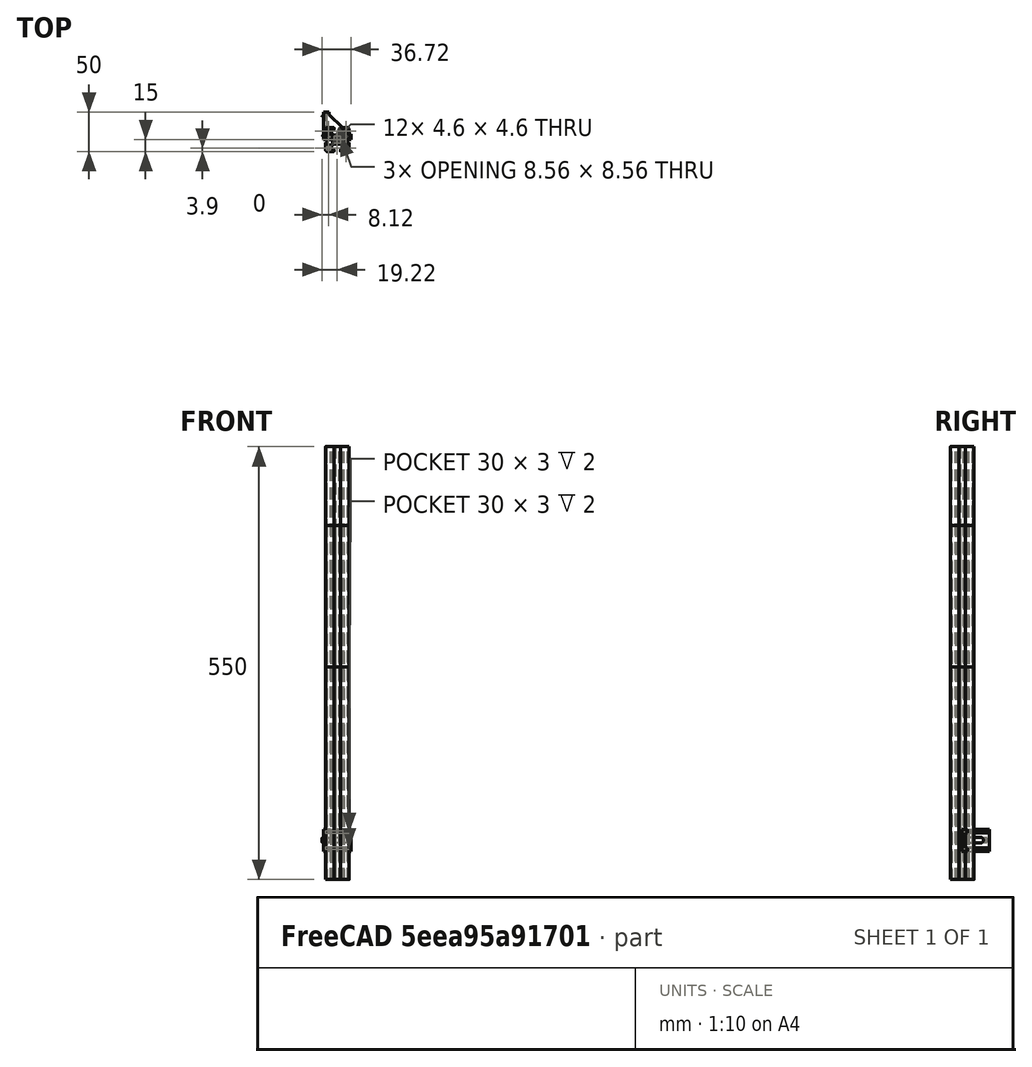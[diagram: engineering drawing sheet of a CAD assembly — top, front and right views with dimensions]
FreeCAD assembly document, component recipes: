
FREECAD ASSEMBLY — COMPONENT RECIPES ("frame")

This assembly document has 67 components, labeled P0..P66 below (a component is one placed body or linked part). 0 of them carry a construction recipe — the FreeCAD feature program that regenerates the part from scratch, quoted from this document or its linked companion documents; the rest are supplied as boundary geometry only. No exploded tour is included for this assembly.
COMPONENT P0 — geometry summary ("30-30 ANGLE BRACKET 002"; no construction recipe available for this part):
  bounding box: 36.7 x 36.7 x 28.0 mm
  tessellated surface: 876 triangles
  volume: 10483 mm^3 (28% of its bounding box)
  symmetry: mirror-symmetric across its y mid-plane
COMPONENT P1 — geometry summary ("30-30 ANGLE BRACKET 003"; no construction recipe available for this part):
  bounding box: 36.7 x 36.7 x 28.0 mm
  tessellated surface: 876 triangles
  volume: 10483 mm^3 (28% of its bounding box)
  symmetry: mirror-symmetric across its y mid-plane
COMPONENT P2 — geometry summary ("30-30 ANGLE BRACKET 004"; no construction recipe available for this part):
  bounding box: 36.7 x 36.7 x 28.0 mm
  tessellated surface: 876 triangles
  volume: 10483 mm^3 (28% of its bounding box)
  symmetry: mirror-symmetric across its y mid-plane
COMPONENT P3 — geometry summary ("30-30 ANGLE BRACKET 005"; no construction recipe available for this part):
  bounding box: 36.7 x 36.7 x 28.0 mm
  tessellated surface: 876 triangles
  volume: 10483 mm^3 (28% of its bounding box)
  symmetry: mirror-symmetric across its y mid-plane
COMPONENT P4 — geometry summary ("30-30 ANGLE BRACKET 006"; no construction recipe available for this part):
  bounding box: 36.7 x 36.7 x 28.0 mm
  tessellated surface: 876 triangles
  volume: 10483 mm^3 (28% of its bounding box)
  symmetry: mirror-symmetric across its y mid-plane
COMPONENT P5 — geometry summary ("30-30 ANGLE BRACKET 007"; no construction recipe available for this part):
  bounding box: 36.7 x 36.7 x 28.0 mm
  tessellated surface: 876 triangles
  volume: 10483 mm^3 (28% of its bounding box)
  symmetry: mirror-symmetric across its y mid-plane
COMPONENT P6 — geometry summary ("30-30 ANGLE BRACKET 008"; no construction recipe available for this part):
  bounding box: 36.7 x 36.7 x 28.0 mm
  tessellated surface: 876 triangles
  volume: 10483 mm^3 (28% of its bounding box)
  symmetry: mirror-symmetric across its y mid-plane
COMPONENT P7 — geometry summary ("30-30 ANGLE BRACKET 009"; no construction recipe available for this part):
  bounding box: 36.7 x 36.7 x 28.0 mm
  tessellated surface: 876 triangles
  volume: 10483 mm^3 (28% of its bounding box)
  symmetry: mirror-symmetric across its y mid-plane
COMPONENT P8 — geometry summary ("30-30 ANGLE BRACKET 010"; no construction recipe available for this part):
  bounding box: 36.7 x 36.7 x 28.0 mm
  tessellated surface: 876 triangles
  volume: 10483 mm^3 (28% of its bounding box)
  symmetry: mirror-symmetric across its y mid-plane
COMPONENT P9 — geometry summary ("30-30 ANGLE BRACKET 011"; no construction recipe available for this part):
  bounding box: 36.7 x 36.7 x 28.0 mm
  tessellated surface: 876 triangles
  volume: 10483 mm^3 (28% of its bounding box)
  symmetry: mirror-symmetric across its y mid-plane
COMPONENT P10 — geometry summary ("30-30 ANGLE BRACKET 012"; no construction recipe available for this part):
  bounding box: 36.7 x 36.7 x 28.0 mm
  tessellated surface: 876 triangles
  volume: 10483 mm^3 (28% of its bounding box)
  symmetry: mirror-symmetric across its y mid-plane
COMPONENT P11 — geometry summary ("30-30 ANGLE BRACKET 013"; no construction recipe available for this part):
  bounding box: 36.7 x 36.7 x 28.0 mm
  tessellated surface: 876 triangles
  volume: 10483 mm^3 (28% of its bounding box)
  symmetry: mirror-symmetric across its y mid-plane
COMPONENT P12 — geometry summary ("30-30 ANGLE BRACKET 014"; no construction recipe available for this part):
  bounding box: 36.7 x 36.7 x 28.0 mm
  tessellated surface: 876 triangles
  volume: 10483 mm^3 (28% of its bounding box)
  symmetry: mirror-symmetric across its y mid-plane
COMPONENT P13 — geometry summary ("30-30 ANGLE BRACKET 015"; no construction recipe available for this part):
  bounding box: 36.7 x 36.7 x 28.0 mm
  tessellated surface: 876 triangles
  volume: 10483 mm^3 (28% of its bounding box)
  symmetry: mirror-symmetric across its y mid-plane
COMPONENT P14 — geometry summary ("30-30 ANGLE BRACKET 016"; no construction recipe available for this part):
  bounding box: 36.7 x 36.7 x 28.0 mm
  tessellated surface: 876 triangles
  volume: 10483 mm^3 (28% of its bounding box)
  symmetry: mirror-symmetric across its y mid-plane
COMPONENT P15 — geometry summary ("30-30 ANGLE BRACKET 017"; no construction recipe available for this part):
  bounding box: 36.7 x 36.7 x 28.0 mm
  tessellated surface: 876 triangles
  volume: 10483 mm^3 (28% of its bounding box)
  symmetry: mirror-symmetric across its y mid-plane
COMPONENT P16 — geometry summary ("30-30 ANGLE BRACKET 018"; no construction recipe available for this part):
  bounding box: 36.7 x 36.7 x 28.0 mm
  tessellated surface: 876 triangles
  volume: 10483 mm^3 (28% of its bounding box)
  symmetry: mirror-symmetric across its y mid-plane
COMPONENT P17 — geometry summary ("30-30 ANGLE BRACKET 019"; no construction recipe available for this part):
  bounding box: 36.7 x 36.7 x 28.0 mm
  tessellated surface: 876 triangles
  volume: 10483 mm^3 (28% of its bounding box)
  symmetry: mirror-symmetric across its y mid-plane
COMPONENT P18 — geometry summary ("30-30 ANGLE BRACKET 020"; no construction recipe available for this part):
  bounding box: 36.7 x 36.7 x 28.0 mm
  tessellated surface: 876 triangles
  volume: 10483 mm^3 (28% of its bounding box)
  symmetry: mirror-symmetric across its y mid-plane
COMPONENT P19 — geometry summary ("30-30 ANGLE BRACKET 021"; no construction recipe available for this part):
  bounding box: 36.7 x 36.7 x 28.0 mm
  tessellated surface: 876 triangles
  volume: 10483 mm^3 (28% of its bounding box)
  symmetry: mirror-symmetric across its y mid-plane
COMPONENT P20 — geometry summary ("30-30 ANGLE BRACKET 022"; no construction recipe available for this part):
  bounding box: 36.7 x 36.7 x 28.0 mm
  tessellated surface: 876 triangles
  volume: 10483 mm^3 (28% of its bounding box)
  symmetry: mirror-symmetric across its y mid-plane
COMPONENT P21 — geometry summary ("30-30 ANGLE BRACKET 023"; no construction recipe available for this part):
  bounding box: 36.7 x 36.7 x 28.0 mm
  tessellated surface: 876 triangles
  volume: 10483 mm^3 (28% of its bounding box)
  symmetry: mirror-symmetric across its y mid-plane
COMPONENT P22 — geometry summary ("30-30 ANGLE BRACKET 024"; no construction recipe available for this part):
  bounding box: 36.7 x 36.7 x 28.0 mm
  tessellated surface: 876 triangles
  volume: 10483 mm^3 (28% of its bounding box)
  symmetry: mirror-symmetric across its y mid-plane
COMPONENT P23 — geometry summary ("30-30 ANGLE BRACKET 025"; no construction recipe available for this part):
  bounding box: 36.7 x 36.7 x 28.0 mm
  tessellated surface: 876 triangles
  volume: 10483 mm^3 (28% of its bounding box)
  symmetry: mirror-symmetric across its y mid-plane
COMPONENT P24 — geometry summary ("30-30 ANGLE BRACKET 026"; no construction recipe available for this part):
  bounding box: 36.7 x 36.7 x 28.0 mm
  tessellated surface: 876 triangles
  volume: 10483 mm^3 (28% of its bounding box)
  symmetry: mirror-symmetric across its y mid-plane
COMPONENT P25 — geometry summary ("30-30 ANGLE BRACKET 027"; no construction recipe available for this part):
  bounding box: 36.7 x 36.7 x 28.0 mm
  tessellated surface: 876 triangles
  volume: 10483 mm^3 (28% of its bounding box)
  symmetry: mirror-symmetric across its y mid-plane
COMPONENT P26 — geometry summary ("30-30 ANGLE BRACKET 028"; no construction recipe available for this part):
  bounding box: 36.7 x 36.7 x 28.0 mm
  tessellated surface: 876 triangles
  volume: 10483 mm^3 (28% of its bounding box)
  symmetry: mirror-symmetric across its y mid-plane
COMPONENT P27 — geometry summary ("30-30 ANGLE BRACKET 029"; no construction recipe available for this part):
  bounding box: 36.7 x 36.7 x 28.0 mm
  tessellated surface: 876 triangles
  volume: 10483 mm^3 (28% of its bounding box)
  symmetry: mirror-symmetric across its y mid-plane
COMPONENT P28 — geometry summary ("30-30 ANGLE BRACKET 030"; no construction recipe available for this part):
  bounding box: 36.7 x 36.7 x 28.0 mm
  tessellated surface: 876 triangles
  volume: 10483 mm^3 (28% of its bounding box)
  symmetry: mirror-symmetric across its y mid-plane
COMPONENT P29 — geometry summary ("30-30 ANGLE BRACKET 031"; no construction recipe available for this part):
  bounding box: 36.7 x 36.7 x 28.0 mm
  tessellated surface: 876 triangles
  volume: 10483 mm^3 (28% of its bounding box)
  symmetry: mirror-symmetric across its y mid-plane
COMPONENT P30 — geometry summary ("30-30 ANGLE BRACKET 032"; no construction recipe available for this part):
  bounding box: 36.7 x 36.7 x 28.0 mm
  tessellated surface: 876 triangles
  volume: 10483 mm^3 (28% of its bounding box)
  symmetry: mirror-symmetric across its y mid-plane
COMPONENT P31 — geometry summary ("30-30 ANGLE BRACKET 033"; no construction recipe available for this part):
  bounding box: 36.7 x 36.7 x 28.0 mm
  tessellated surface: 876 triangles
  volume: 10483 mm^3 (28% of its bounding box)
  symmetry: mirror-symmetric across its y mid-plane
COMPONENT P32 — geometry summary ("30-30 ANGLE BRACKET 034"; no construction recipe available for this part):
  bounding box: 36.7 x 36.7 x 28.0 mm
  tessellated surface: 876 triangles
  volume: 10483 mm^3 (28% of its bounding box)
  symmetry: mirror-symmetric across its y mid-plane
COMPONENT P33 — geometry summary ("30-30 ANGLE BRACKET 035"; no construction recipe available for this part):
  bounding box: 36.7 x 36.7 x 28.0 mm
  tessellated surface: 876 triangles
  volume: 10483 mm^3 (28% of its bounding box)
  symmetry: mirror-symmetric across its y mid-plane
COMPONENT P34 — geometry summary ("30-30 ANGLE BRACKET 036"; no construction recipe available for this part):
  bounding box: 36.7 x 36.7 x 28.0 mm
  tessellated surface: 876 triangles
  volume: 10483 mm^3 (28% of its bounding box)
  symmetry: mirror-symmetric across its y mid-plane
COMPONENT P35 — geometry summary ("30-30 ANGLE BRACKET 037"; no construction recipe available for this part):
  bounding box: 36.7 x 36.7 x 28.0 mm
  tessellated surface: 876 triangles
  volume: 10483 mm^3 (28% of its bounding box)
  symmetry: mirror-symmetric across its y mid-plane
COMPONENT P36 — geometry summary ("30-30 ANGLE BRACKET 038"; no construction recipe available for this part):
  bounding box: 36.7 x 36.7 x 28.0 mm
  tessellated surface: 876 triangles
  volume: 10483 mm^3 (28% of its bounding box)
  symmetry: mirror-symmetric across its y mid-plane
COMPONENT P37 — geometry summary ("30-30 ANGLE BRACKET 039"; no construction recipe available for this part):
  bounding box: 36.7 x 36.7 x 28.0 mm
  tessellated surface: 876 triangles
  volume: 10483 mm^3 (28% of its bounding box)
  symmetry: mirror-symmetric across its y mid-plane
COMPONENT P38 — geometry summary ("30-30 ANGLE BRACKET 040"; no construction recipe available for this part):
  bounding box: 36.7 x 36.7 x 28.0 mm
  tessellated surface: 876 triangles
  volume: 10483 mm^3 (28% of its bounding box)
  symmetry: mirror-symmetric across its y mid-plane
COMPONENT P39 — geometry summary ("30-30 ANGLE BRACKET 041"; no construction recipe available for this part):
  bounding box: 36.7 x 36.7 x 28.0 mm
  tessellated surface: 876 triangles
  volume: 10483 mm^3 (28% of its bounding box)
  symmetry: mirror-symmetric across its y mid-plane
COMPONENT P40 — geometry summary ("30-30 ANGLE BRACKET 042"; no construction recipe available for this part):
  bounding box: 36.7 x 36.7 x 28.0 mm
  tessellated surface: 876 triangles
  volume: 10483 mm^3 (28% of its bounding box)
  symmetry: mirror-symmetric across its y mid-plane
COMPONENT P41 — geometry summary ("30-30 ANGLE BRACKET 043"; no construction recipe available for this part):
  bounding box: 36.7 x 36.7 x 28.0 mm
  tessellated surface: 876 triangles
  volume: 10483 mm^3 (28% of its bounding box)
  symmetry: mirror-symmetric across its y mid-plane
COMPONENT P42 — geometry summary ("30-30 ANGLE BRACKET 044"; no construction recipe available for this part):
  bounding box: 36.7 x 36.7 x 28.0 mm
  tessellated surface: 876 triangles
  volume: 10483 mm^3 (28% of its bounding box)
  symmetry: mirror-symmetric across its y mid-plane
COMPONENT P43 — geometry summary ("30-30 ANGLE BRACKET 045"; no construction recipe available for this part):
  bounding box: 36.7 x 36.7 x 28.0 mm
  tessellated surface: 876 triangles
  volume: 10483 mm^3 (28% of its bounding box)
  symmetry: mirror-symmetric across its y mid-plane
COMPONENT P44 — geometry summary ("30-30 ANGLE BRACKET 046"; no construction recipe available for this part):
  bounding box: 36.7 x 36.7 x 28.0 mm
  tessellated surface: 876 triangles
  volume: 10483 mm^3 (28% of its bounding box)
  symmetry: mirror-symmetric across its y mid-plane
COMPONENT P45 — geometry summary ("30-30 ANGLE BRACKET 047"; no construction recipe available for this part):
  bounding box: 36.7 x 36.7 x 28.0 mm
  tessellated surface: 876 triangles
  volume: 10483 mm^3 (28% of its bounding box)
  symmetry: mirror-symmetric across its y mid-plane
COMPONENT P46 — geometry summary ("30x30 270 002"; no construction recipe available for this part):
  bounding box: 270.0 x 30.0 x 30.0 mm
  tessellated surface: 1,312 triangles
  volume: 84097 mm^3 (35% of its bounding box)
  symmetry: 4-fold rotationally symmetric about the x axis; 2-fold rotationally symmetric about the y axis; 2-fold rotationally symmetric about the z axis; mirror-symmetric across its x mid-plane, y mid-plane, z mid-plane
COMPONENT P47 — geometry summary ("30x30 270 003"; no construction recipe available for this part):
  bounding box: 270.0 x 30.0 x 30.0 mm
  tessellated surface: 1,312 triangles
  volume: 84097 mm^3 (35% of its bounding box)
  symmetry: 4-fold rotationally symmetric about the x axis; 2-fold rotationally symmetric about the y axis; 2-fold rotationally symmetric about the z axis; mirror-symmetric across its x mid-plane, y mid-plane, z mid-plane
COMPONENT P48 — geometry summary ("30x30 450 005"; no construction recipe available for this part):
  bounding box: 450.0 x 30.0 x 30.0 mm
  tessellated surface: 1,312 triangles
  volume: 140161 mm^3 (35% of its bounding box)
  symmetry: 2-fold rotationally symmetric about the x axis; 2-fold rotationally symmetric about the y axis; 4-fold rotationally symmetric about the z axis; mirror-symmetric across its x mid-plane, y mid-plane, z mid-plane
COMPONENT P49 — geometry summary ("30x30 450 006"; no construction recipe available for this part):
  bounding box: 450.0 x 30.0 x 30.0 mm
  tessellated surface: 1,312 triangles
  volume: 140161 mm^3 (35% of its bounding box)
  symmetry: 2-fold rotationally symmetric about the x axis; 2-fold rotationally symmetric about the y axis; 4-fold rotationally symmetric about the z axis; mirror-symmetric across its x mid-plane, y mid-plane, z mid-plane
COMPONENT P50 — geometry summary ("30x30 450 007"; no construction recipe available for this part):
  bounding box: 450.0 x 30.0 x 30.0 mm
  tessellated surface: 1,312 triangles
  volume: 140161 mm^3 (35% of its bounding box)
  symmetry: 2-fold rotationally symmetric about the x axis; 2-fold rotationally symmetric about the y axis; 4-fold rotationally symmetric about the z axis; mirror-symmetric across its x mid-plane, y mid-plane, z mid-plane
COMPONENT P51 — geometry summary ("30x30 450 008"; no construction recipe available for this part):
  bounding box: 450.0 x 30.0 x 30.0 mm
  tessellated surface: 1,312 triangles
  volume: 140161 mm^3 (35% of its bounding box)
  symmetry: 2-fold rotationally symmetric about the x axis; 2-fold rotationally symmetric about the y axis; 4-fold rotationally symmetric about the z axis; mirror-symmetric across its x mid-plane, y mid-plane, z mid-plane
COMPONENT P52 — geometry summary ("30x30 450 009"; no construction recipe available for this part):
  bounding box: 450.0 x 30.0 x 30.0 mm
  tessellated surface: 1,312 triangles
  volume: 140161 mm^3 (35% of its bounding box)
  symmetry: 2-fold rotationally symmetric about the x axis; 2-fold rotationally symmetric about the y axis; 4-fold rotationally symmetric about the z axis; mirror-symmetric across its x mid-plane, y mid-plane, z mid-plane
COMPONENT P53 — geometry summary ("30x30 450 010"; no construction recipe available for this part):
  bounding box: 450.0 x 30.0 x 30.0 mm
  tessellated surface: 1,312 triangles
  volume: 140161 mm^3 (35% of its bounding box)
  symmetry: 2-fold rotationally symmetric about the x axis; 2-fold rotationally symmetric about the y axis; 4-fold rotationally symmetric about the z axis; mirror-symmetric across its x mid-plane, y mid-plane, z mid-plane
COMPONENT P54 — geometry summary ("30x30 450 011"; no construction recipe available for this part):
  bounding box: 450.0 x 30.0 x 30.0 mm
  tessellated surface: 1,312 triangles
  volume: 140161 mm^3 (35% of its bounding box)
  symmetry: 2-fold rotationally symmetric about the x axis; 2-fold rotationally symmetric about the y axis; 4-fold rotationally symmetric about the z axis; mirror-symmetric across its x mid-plane, y mid-plane, z mid-plane
COMPONENT P55 — geometry summary ("30x30 450 012"; no construction recipe available for this part):
  bounding box: 450.0 x 30.0 x 30.0 mm
  tessellated surface: 1,312 triangles
  volume: 140161 mm^3 (35% of its bounding box)
  symmetry: 2-fold rotationally symmetric about the x axis; 2-fold rotationally symmetric about the y axis; 4-fold rotationally symmetric about the z axis; mirror-symmetric across its x mid-plane, y mid-plane, z mid-plane
COMPONENT P56 — geometry summary ("30x30 450 013"; no construction recipe available for this part):
  bounding box: 450.0 x 30.0 x 30.0 mm
  tessellated surface: 1,312 triangles
  volume: 140161 mm^3 (35% of its bounding box)
  symmetry: 2-fold rotationally symmetric about the x axis; 2-fold rotationally symmetric about the y axis; 4-fold rotationally symmetric about the z axis; mirror-symmetric across its x mid-plane, y mid-plane, z mid-plane
COMPONENT P57 — geometry summary ("30x30 450 014"; no construction recipe available for this part):
  bounding box: 450.0 x 30.0 x 30.0 mm
  tessellated surface: 1,312 triangles
  volume: 140161 mm^3 (35% of its bounding box)
  symmetry: 2-fold rotationally symmetric about the x axis; 2-fold rotationally symmetric about the y axis; 4-fold rotationally symmetric about the z axis; mirror-symmetric across its x mid-plane, y mid-plane, z mid-plane
COMPONENT P58 — geometry summary ("30x30 450 015"; no construction recipe available for this part):
  bounding box: 450.0 x 30.0 x 30.0 mm
  tessellated surface: 1,312 triangles
  volume: 140161 mm^3 (35% of its bounding box)
  symmetry: 2-fold rotationally symmetric about the x axis; 2-fold rotationally symmetric about the y axis; 4-fold rotationally symmetric about the z axis; mirror-symmetric across its x mid-plane, y mid-plane, z mid-plane
COMPONENT P59 — geometry summary ("30x30 450 016"; no construction recipe available for this part):
  bounding box: 450.0 x 30.0 x 30.0 mm
  tessellated surface: 1,312 triangles
  volume: 140161 mm^3 (35% of its bounding box)
  symmetry: 2-fold rotationally symmetric about the x axis; 2-fold rotationally symmetric about the y axis; 4-fold rotationally symmetric about the z axis; mirror-symmetric across its x mid-plane, y mid-plane, z mid-plane
COMPONENT P60 — geometry summary ("30x30 450 002"; no construction recipe available for this part):
  bounding box: 450.0 x 30.0 x 30.0 mm
  tessellated surface: 1,312 triangles
  volume: 140161 mm^3 (35% of its bounding box)
  symmetry: 2-fold rotationally symmetric about the x axis; 2-fold rotationally symmetric about the y axis; 4-fold rotationally symmetric about the z axis; mirror-symmetric across its x mid-plane, y mid-plane, z mid-plane
COMPONENT P61 — geometry summary ("30x30 550 003"; no construction recipe available for this part):
  bounding box: 550.0 x 30.0 x 30.0 mm
  tessellated surface: 1,312 triangles
  volume: 171308 mm^3 (35% of its bounding box)
  symmetry: 4-fold rotationally symmetric about the x axis; 2-fold rotationally symmetric about the y axis; 2-fold rotationally symmetric about the z axis; mirror-symmetric across its x mid-plane, y mid-plane, z mid-plane
COMPONENT P62 — geometry summary ("30x30 550 004"; no construction recipe available for this part):
  bounding box: 550.0 x 30.0 x 30.0 mm
  tessellated surface: 1,312 triangles
  volume: 171308 mm^3 (35% of its bounding box)
  symmetry: 4-fold rotationally symmetric about the x axis; 2-fold rotationally symmetric about the y axis; 2-fold rotationally symmetric about the z axis; mirror-symmetric across its x mid-plane, y mid-plane, z mid-plane
COMPONENT P63 — geometry summary ("30x30 550 005"; no construction recipe available for this part):
  bounding box: 550.0 x 30.0 x 30.0 mm
  tessellated surface: 1,312 triangles
  volume: 171308 mm^3 (35% of its bounding box)
  symmetry: 4-fold rotationally symmetric about the x axis; 2-fold rotationally symmetric about the y axis; 2-fold rotationally symmetric about the z axis; mirror-symmetric across its x mid-plane, y mid-plane, z mid-plane
COMPONENT P64 — geometry summary ("30x30 550 002"; no construction recipe available for this part):
  bounding box: 550.0 x 30.0 x 30.0 mm
  tessellated surface: 1,312 triangles
  volume: 171308 mm^3 (35% of its bounding box)
  symmetry: 4-fold rotationally symmetric about the x axis; 2-fold rotationally symmetric about the y axis; 2-fold rotationally symmetric about the z axis; mirror-symmetric across its x mid-plane, y mid-plane, z mid-plane
COMPONENT P65 — geometry summary ("30x30 450 003"; no construction recipe available for this part):
  bounding box: 450.0 x 30.0 x 30.0 mm
  tessellated surface: 1,312 triangles
  volume: 140161 mm^3 (35% of its bounding box)
  symmetry: 2-fold rotationally symmetric about the x axis; 2-fold rotationally symmetric about the y axis; 4-fold rotationally symmetric about the z axis; mirror-symmetric across its x mid-plane, y mid-plane, z mid-plane
COMPONENT P66 — geometry summary ("30x30 450 004"; no construction recipe available for this part):
  bounding box: 450.0 x 30.0 x 30.0 mm
  tessellated surface: 1,312 triangles
  volume: 140161 mm^3 (35% of its bounding box)
  symmetry: 2-fold rotationally symmetric about the x axis; 2-fold rotationally symmetric about the y axis; 4-fold rotationally symmetric about the z axis; mirror-symmetric across its x mid-plane, y mid-plane, z mid-plane
PROVENANCE & LICENSES
A FreeCAD (.FCStd) document from a public repository crawl; recipes are the document's own serialized feature recipes (and, for linked parts, companion documents' recipes).
License: other.
